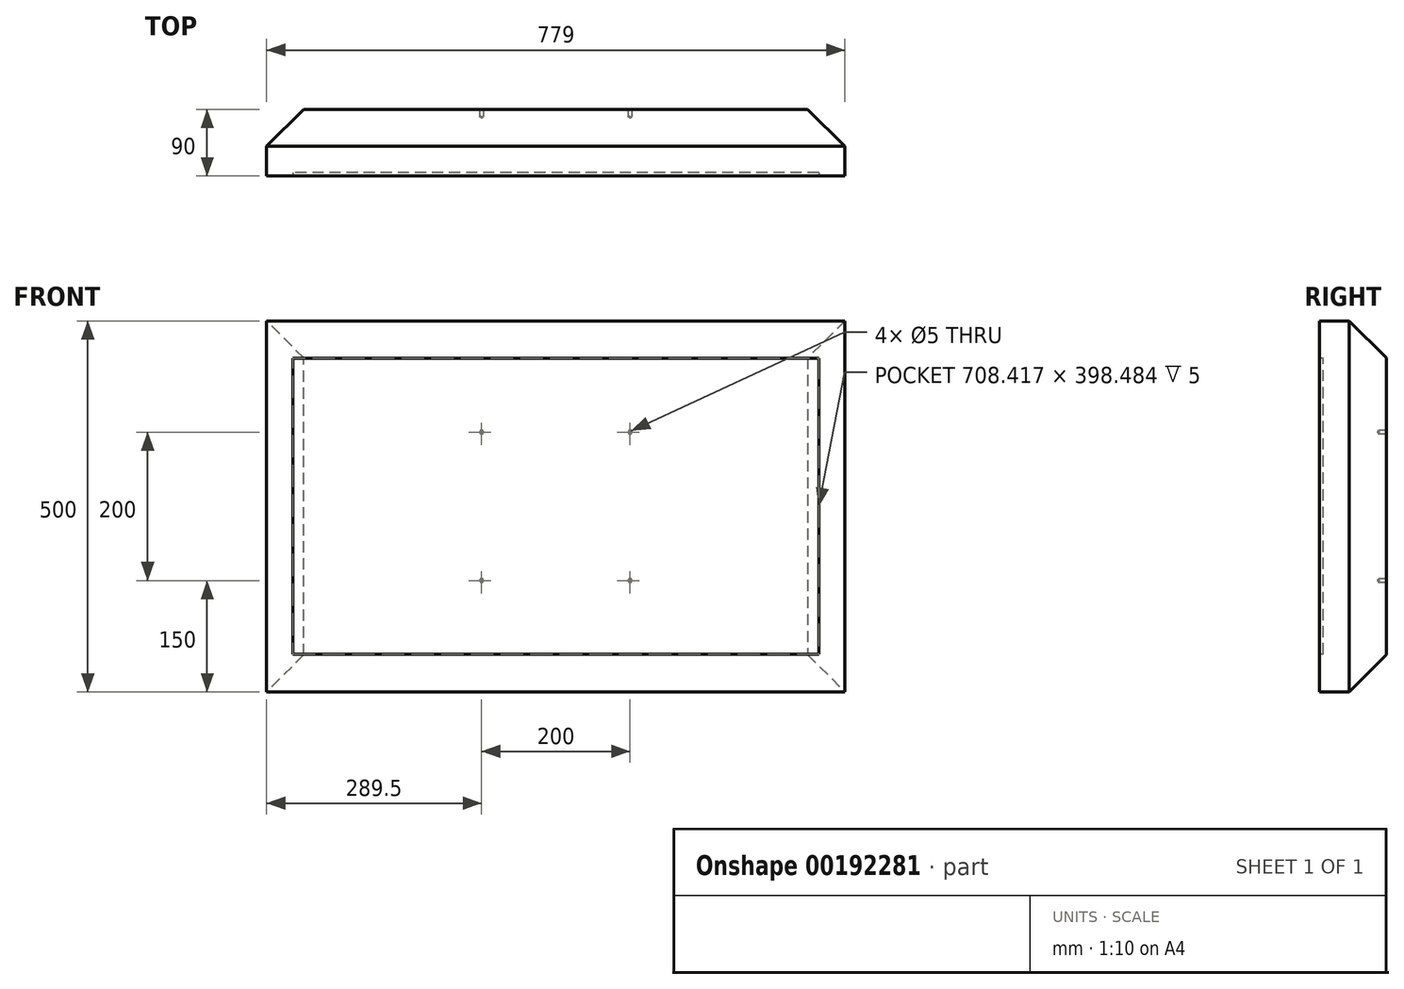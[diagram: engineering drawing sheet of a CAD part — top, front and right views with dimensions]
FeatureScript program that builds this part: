
annotation { "Feature Type Name" : "Feature", "Feature Type Description" : "" }
export const myFeature = defineFeature(function(context is Context, id is Id, definition is map)
    precondition{}
    {
        {
            var Q0;
            Q0=qCreatedBy(makeId("Front.planeOp"),FACE);
            var sketch = newSketch(context, id + "F0", { "sketchPlane" : qUnion([Q0])});
            skLineSegment(sketch, "E0.bottom", {"start": v(389.5, 250) * mm, "end": v(-389.5, 250) * mm});
            skLineSegment(sketch, "E0.top", {"start": v(389.5, -250) * mm, "end": v(-389.5, -250) * mm});
            skLineSegment(sketch, "E0.left", {"start": v(389.5, 250) * mm, "end": v(389.5, -250) * mm});
            skLineSegment(sketch, "E0.right", {"start": v(-389.5, 250) * mm, "end": v(-389.5, -250) * mm});
            skPoint(sketch, "E0.middle", {"position": v(0, 0) * mm});
            skSolve(sketch);
        }
        {
            var Q0;
            Q0=qSketchRegion(id+"F0",true);
            extrude(context, id + "F1", {"entities" : qUnion([Q0]), "depth" : 90 * mm});
        }
        {
            var Q0;
            Q0=makeQuery(id+"F1.opExtrude","CAP_FACE",FACE,{"disambiguationData":[OSD([sQuery(id+"F0.wireOp",EDGE,"E0.bottom"),sQuery(id+"F0.wireOp",EDGE,"E0.top"),sQuery(id+"F0.wireOp",EDGE,"E0.left"),sQuery(id+"F0.wireOp",EDGE,"E0.right")])],"isStart":true});
            chamfer(context, id + "F2", {"entities" : qUnion([Q0]), "width" : 50 * mm, "tangentPropagation" : true});
        }
        {
            var Q0;
            Q0=makeQuery(id+"F1.opExtrude","CAP_FACE",FACE,{"disambiguationData":[OSD([sQuery(id+"F0.wireOp",EDGE,"E0.bottom"),sQuery(id+"F0.wireOp",EDGE,"E0.top"),sQuery(id+"F0.wireOp",EDGE,"E0.left"),sQuery(id+"F0.wireOp",EDGE,"E0.right")])],"isStart":false});
            var sketch = newSketch(context, id + "F3", { "sketchPlane" : qUnion([Q0])});
            skLineSegment(sketch, "E1.bottom", {"start": v(354.2, -199.24) * mm, "end": v(-354.2, -199.24) * mm});
            skLineSegment(sketch, "E1.top", {"start": v(354.2, 199.24) * mm, "end": v(-354.2, 199.24) * mm});
            skLineSegment(sketch, "E1.left", {"start": v(354.2, -199.24) * mm, "end": v(354.2, 199.24) * mm});
            skLineSegment(sketch, "E1.right", {"start": v(-354.2, -199.24) * mm, "end": v(-354.2, 199.24) * mm});
            skPoint(sketch, "E1.middle", {"position": v(0, 0) * mm});
            skLineSegment(sketch, "E2", {"start": v(-354.2, 136.72) * mm, "end": v(-309.93, 136.72) * mm, "construction": true});
            skLineSegment(sketch, "E3", {"start": v(-309.93, 136.72) * mm, "end": v(-265.66, 136.72) * mm, "construction": true});
            skLineSegment(sketch, "E4", {"start": v(-265.66, 136.72) * mm, "end": v(-221.38, 136.72) * mm, "construction": true});
            skLineSegment(sketch, "E5", {"start": v(-221.38, 136.72) * mm, "end": v(-177.1, 136.72) * mm, "construction": true});
            skLineSegment(sketch, "E6", {"start": v(-177.1, 136.72) * mm, "end": v(-132.83, 136.72) * mm, "construction": true});
            skLineSegment(sketch, "E7", {"start": v(-132.83, 136.72) * mm, "end": v(-88.55, 136.72) * mm, "construction": true});
            skLineSegment(sketch, "E8", {"start": v(-88.55, 136.72) * mm, "end": v(-44.28, 136.72) * mm, "construction": true});
            skLineSegment(sketch, "E9", {"start": v(-44.28, 136.72) * mm, "end": v(0, 136.72) * mm, "construction": true});
            skLineSegment(sketch, "E10", {"start": v(0, 136.72) * mm, "end": v(44.28, 136.72) * mm, "construction": true});
            skLineSegment(sketch, "E11", {"start": v(44.28, 136.72) * mm, "end": v(88.55, 136.72) * mm, "construction": true});
            skLineSegment(sketch, "E12", {"start": v(88.55, 136.72) * mm, "end": v(132.83, 136.72) * mm, "construction": true});
            skLineSegment(sketch, "E13", {"start": v(132.83, 136.72) * mm, "end": v(177.1, 136.72) * mm, "construction": true});
            skLineSegment(sketch, "E14", {"start": v(177.1, 136.72) * mm, "end": v(221.38, 136.72) * mm, "construction": true});
            skLineSegment(sketch, "E15", {"start": v(221.38, 136.72) * mm, "end": v(265.66, 136.72) * mm, "construction": true});
            skLineSegment(sketch, "E16", {"start": v(265.66, 136.72) * mm, "end": v(309.93, 136.72) * mm, "construction": true});
            skLineSegment(sketch, "E17", {"start": v(309.93, 136.72) * mm, "end": v(354.2, 136.72) * mm, "construction": true});
            skLineSegment(sketch, "E18", {"start": v(172.38, 199.24) * mm, "end": v(172.38, 154.97) * mm, "construction": true});
            skLineSegment(sketch, "E19", {"start": v(172.38, 154.97) * mm, "end": v(172.38, 110.7) * mm, "construction": true});
            skLineSegment(sketch, "E20", {"start": v(172.38, 110.7) * mm, "end": v(172.38, 66.41) * mm, "construction": true});
            skLineSegment(sketch, "E21", {"start": v(172.38, 66.41) * mm, "end": v(172.38, 22.14) * mm, "construction": true});
            skLineSegment(sketch, "E22", {"start": v(172.38, 22.14) * mm, "end": v(172.38, -22.14) * mm, "construction": true});
            skLineSegment(sketch, "E23", {"start": v(172.38, -22.14) * mm, "end": v(172.38, -66.41) * mm, "construction": true});
            skLineSegment(sketch, "E24", {"start": v(172.38, -66.41) * mm, "end": v(172.38, -110.7) * mm, "construction": true});
            skLineSegment(sketch, "E25", {"start": v(172.38, -110.7) * mm, "end": v(172.38, -154.97) * mm, "construction": true});
            skLineSegment(sketch, "E26", {"start": v(172.38, -154.97) * mm, "end": v(172.38, -199.24) * mm, "construction": true});
            skSolve(sketch);
        }
        {
            var Q0;
            Q0=makeQuery(id+"F3.imprint","IMPRINT",FACE,{"disambiguationData":[TD([[makeQuery(id+"F3.imprint","IMPRINT",EDGE,{"derivedFrom":sQuery(id+"F3.wireOp",EDGE,"E1.bottom")}),-1.0]])]});
            extrude(context, id + "F4", {"entities" : qUnion([Q0]), "operationType" : NewBodyOperationType.REMOVE, "oppositeDirection" : true, "depth" : 5 * mm});
        }
        {
            var Q0;
            Q0=makeQuery(id+"F1.opExtrude","CAP_FACE",FACE,{"disambiguationData":[OSD([sQuery(id+"F0.wireOp",EDGE,"E0.bottom"),sQuery(id+"F0.wireOp",EDGE,"E0.top"),sQuery(id+"F0.wireOp",EDGE,"E0.left"),sQuery(id+"F0.wireOp",EDGE,"E0.right")])],"isStart":true});
            var sketch = newSketch(context, id + "F5", { "sketchPlane" : qUnion([Q0])});
            skLineSegment(sketch, "E27.bottom", {"start": v(100, -100) * mm, "end": v(-100, -100) * mm, "construction": true});
            skLineSegment(sketch, "E27.top", {"start": v(100, 100) * mm, "end": v(-100, 100) * mm, "construction": true});
            skLineSegment(sketch, "E27.left", {"start": v(100, -100) * mm, "end": v(100, 100) * mm, "construction": true});
            skLineSegment(sketch, "E27.right", {"start": v(-100, -100) * mm, "end": v(-100, 100) * mm, "construction": true});
            skPoint(sketch, "E27.middle", {"position": v(0, 0) * mm});
            skSolve(sketch);
        }
        {
            var Q0;
            Q0=sQuery(id+"F5.wireOp",VERTEX,"E27.right.end");
            var Q1;
            Q1=sQuery(id+"F5.wireOp",VERTEX,"E27.left.end");
            var Q2;
            Q2=sQuery(id+"F5.wireOp",VERTEX,"E27.right.start");
            var Q3;
            Q3=sQuery(id+"F5.wireOp",VERTEX,"E27.bottom.start");
            var Q4;
            Q4=makeQuery(id+"F1.opExtrude","SWEPT_BODY",BODY,{"disambiguationData":[OSD([sQuery(id+"F0.wireOp",EDGE,"E0.bottom"),sQuery(id+"F0.wireOp",EDGE,"E0.top"),sQuery(id+"F0.wireOp",EDGE,"E0.left"),sQuery(id+"F0.wireOp",EDGE,"E0.right")])]});
            hole(context, id + "F6", {"style" : HoleStyle.SIMPLE, "endStyle" : HoleEndStyle.BLIND, "standardTappedOrClearance" : lookupTablePath({ "standard" : "ISO", "engagement" : "75%", "pitch" : "1 mm", "size" : "M6", "type" : "Tapped" }), "standardBlindInLast" : lookupTablePath({ "standard" : "ISO", "engagement" : "75%", "pitch" : "1 mm", "size" : "M6", "type" : "Tapped" }), "holeDiameter" : 5 * mm, "holeDepth" : 10 * mm, "locations" : qUnion([Q0, Q1, Q2, Q3]), "scope" : qUnion([Q4]), "majorDiameter" : 6 * mm, "startStyle" : HoleStartStyle.SKETCH});
        }
    });
